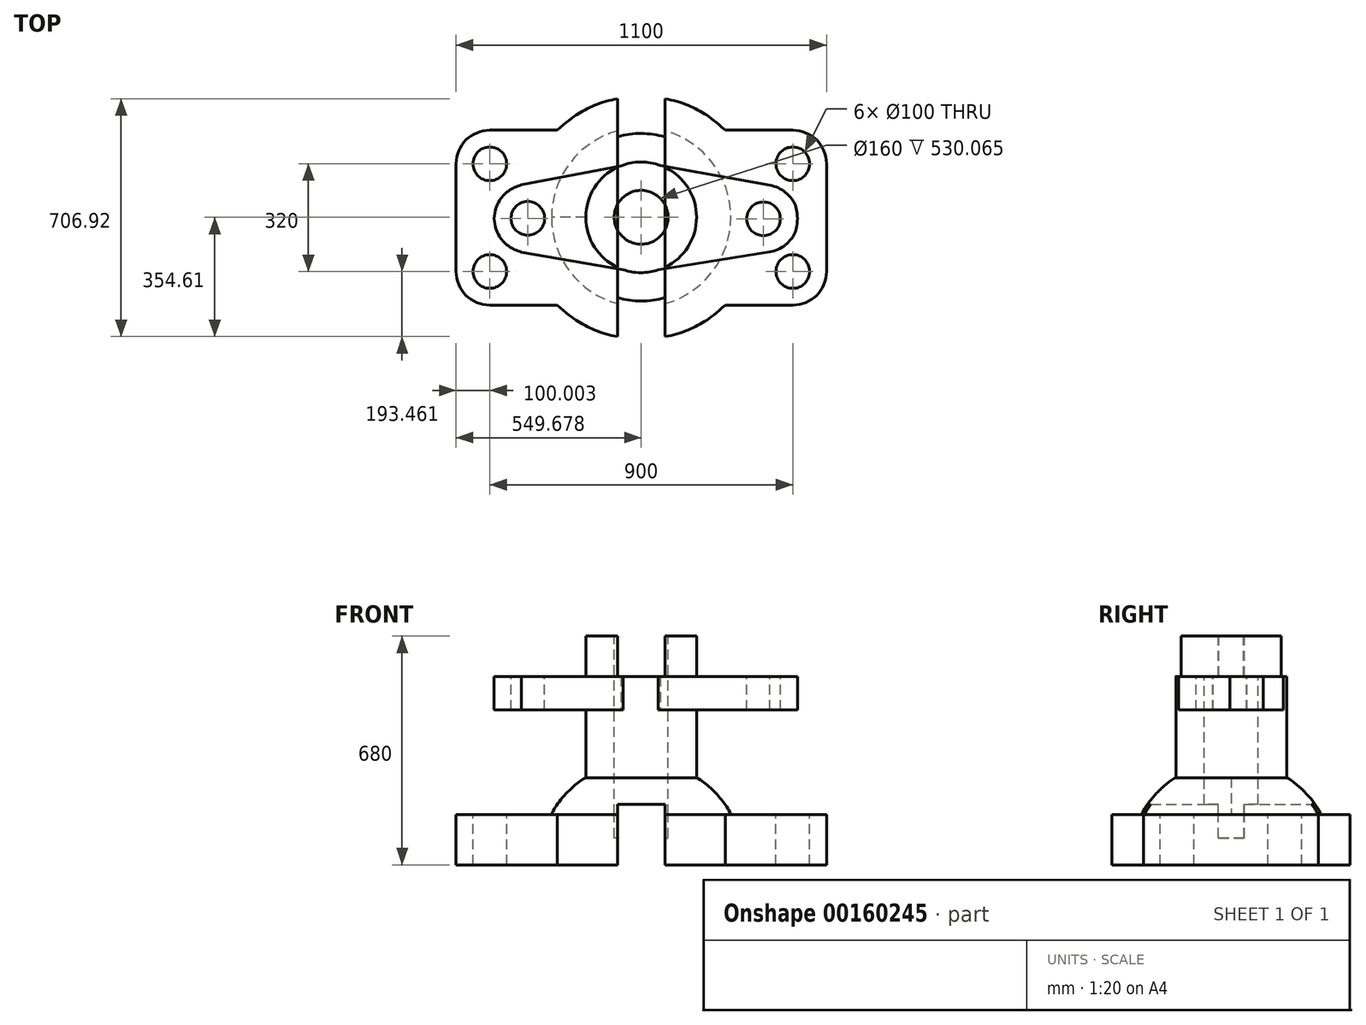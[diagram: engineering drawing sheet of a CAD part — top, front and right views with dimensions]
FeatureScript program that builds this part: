
annotation { "Feature Type Name" : "Feature", "Feature Type Description" : "" }
export const myFeature = defineFeature(function(context is Context, id is Id, definition is map)
    precondition{}
    {
        {
            var Q0;
            Q0=qCreatedBy(makeId("Top.planeOp"),FACE);
            var sketch = newSketch(context, id + "F0", { "sketchPlane" : qUnion([Q0])});
            skLineSegment(sketch, "E0.bottom", {"start": v(-555.83, 304.85) * mm, "end": v(544.17, 304.85) * mm});
            skLineSegment(sketch, "E0.top", {"start": v(-555.83, -215.15) * mm, "end": v(544.17, -215.15) * mm});
            skLineSegment(sketch, "E0.left", {"start": v(-555.83, 304.85) * mm, "end": v(-555.83, -215.15) * mm});
            skLineSegment(sketch, "E0.right", {"start": v(544.17, 304.85) * mm, "end": v(544.17, -215.15) * mm});
            skLineSegment(sketch, "E1", {"start": v(-555.83, 304.85) * mm, "end": v(-555.83, 365.16) * mm});
            skLineSegment(sketch, "E2", {"start": v(-76.07, 304.85) * mm, "end": v(-76.07, 398.31) * mm});
            skFitSpline(sketch, "E3", {"points": [v(-76.07, 398.31) * mm, v(-167.84, 368.02) * mm, v(-255.04, 304.85) * mm], "startDerivative": vector(-216.42, -35.21) * mm, "endDerivative": vector(-219.3, -200.67) * mm});
            skLineSegment(sketch, "E4", {"start": v(-5.83, 365.16) * mm, "end": v(-5.83, 347.73) * mm});
            skLineSegment(sketch, "E5.MirrorCS", {"start": v(64.42, 304.85) * mm, "end": v(64.42, 398.31) * mm});
            skFitSpline(sketch, "E6.MirrorCS", {"points": [v(64.42, 398.31) * mm, v(156.19, 368.02) * mm, v(243.39, 304.85) * mm], "startDerivative": vector(216.42, -35.21) * mm, "endDerivative": vector(219.3, -200.67) * mm});
            skLineSegment(sketch, "E7", {"start": v(544.17, 304.85) * mm, "end": v(591.2, 304.85) * mm});
            skLineSegment(sketch, "E8", {"start": v(591.2, 304.85) * mm, "end": v(591.2, 44.85) * mm});
            skLineSegment(sketch, "E9", {"start": v(591.2, 44.85) * mm, "end": v(627.35, 44.85) * mm});
            skLineSegment(sketch, "E10.MirrorCS", {"start": v(64.42, -215.15) * mm, "end": v(64.42, -308.61) * mm});
            skLineSegment(sketch, "E11.MirrorCS", {"start": v(-76.07, -215.15) * mm, "end": v(-76.07, -308.61) * mm});
            skFitSpline(sketch, "E12.MirrorCS", {"points": [v(-76.07, -308.61) * mm, v(-167.84, -278.32) * mm, v(-255.04, -215.15) * mm], "startDerivative": vector(-216.42, 35.21) * mm, "endDerivative": vector(-219.3, 200.67) * mm});
            skFitSpline(sketch, "E13.MirrorCS", {"points": [v(64.42, -308.61) * mm, v(156.19, -278.32) * mm, v(243.39, -215.15) * mm], "startDerivative": vector(216.42, 35.21) * mm, "endDerivative": vector(219.3, 200.67) * mm});
            skSolve(sketch);
        }
        {
            var Q0;
            Q0 = qSketchRegion(id + "F0", true);
            extrude(context, id + "F1", {"entities" : qUnion([Q0]), "depth" : 150 * mm});
        }
        {
            var Q0;
            Q0=makeQuery(id+"F1.opExtrude","SWEPT_EDGE",EDGE,{"disambiguationData":[OSD([sQuery(id+"F0.wireOp",EDGE,"E0.top"),sQuery(id+"F0.wireOp",EDGE,"E0.left")])]});
            fillet(context, id + "F2", {"entities" : qUnion([Q0]), "radius" : 100 * mm, "tangentPropagation" : true, "allowEdgeOverflow" : false});
        }
        {
            var Q0;
            Q0=makeQuery(id+"F1.opExtrude","SWEPT_EDGE",EDGE,{"disambiguationData":[OSD([sQuery(id+"F0.wireOp",EDGE,"E0.bottom"),sQuery(id+"F0.wireOp",EDGE,"E0.left")])]});
            fillet(context, id + "F3", {"entities" : qUnion([Q0]), "radius" : 100 * mm, "tangentPropagation" : true, "allowEdgeOverflow" : false});
        }
        {
            var Q0;
            Q0=makeQuery(id+"F1.opExtrude","SWEPT_EDGE",EDGE,{"disambiguationData":[OSD([sQuery(id+"F0.wireOp",EDGE,"E0.bottom"),sQuery(id+"F0.wireOp",EDGE,"E0.right")])]});
            fillet(context, id + "F4", {"entities" : qUnion([Q0]), "radius" : 100 * mm, "tangentPropagation" : true, "allowEdgeOverflow" : false});
        }
        {
            var Q0;
            Q0=makeQuery(id+"F1.opExtrude","SWEPT_EDGE",EDGE,{"disambiguationData":[OSD([sQuery(id+"F0.wireOp",EDGE,"E0.top"),sQuery(id+"F0.wireOp",EDGE,"E0.right")])]});
            fillet(context, id + "F5", {"entities" : qUnion([Q0]), "radius" : 100 * mm, "tangentPropagation" : true, "allowEdgeOverflow" : false});
        }
        {
            var Q0;
            Q0=makeQuery(id+"F1.opExtrude","CAP_FACE",FACE,{"disambiguationData":[OSD([sQuery(id+"F0.wireOp",EDGE,"E0.bottom"),sQuery(id+"F0.wireOp",EDGE,"E0.top"),sQuery(id+"F0.wireOp",EDGE,"E0.left"),sQuery(id+"F0.wireOp",EDGE,"E0.right"),sQuery(id+"F0.wireOp",EDGE,"E2"),sQuery(id+"F0.wireOp",EDGE,"E3"),sQuery(id+"F0.wireOp",EDGE,"E5.MirrorCS"),sQuery(id+"F0.wireOp",EDGE,"E6.MirrorCS"),sQuery(id+"F0.wireOp",EDGE,"E10.MirrorCS"),sQuery(id+"F0.wireOp",EDGE,"E11.MirrorCS"),sQuery(id+"F0.wireOp",EDGE,"E12.MirrorCS"),sQuery(id+"F0.wireOp",EDGE,"E13.MirrorCS")])],"isStart":false});
            var sketch = newSketch(context, id + "F6", { "sketchPlane" : qUnion([Q0])});
            skCircle(sketch, "E14", {"center": v(-455.83, -115.15) * mm, "radius": 50 * mm});
            skCircle(sketch, "E15.MirrorC", {"center": v(-455.83, 204.85) * mm, "radius": 50 * mm});
            skCircle(sketch, "E16.MirrorC", {"center": v(444.17, 204.85) * mm, "radius": 50 * mm});
            skCircle(sketch, "E17.MirrorC", {"center": v(444.17, -115.15) * mm, "radius": 50 * mm});
            skLineSegment(sketch, "E18.bottom", {"start": v(64.42, 304.85) * mm, "end": v(-76.07, 304.85) * mm});
            skLineSegment(sketch, "E18.top", {"start": v(64.42, -215.15) * mm, "end": v(-76.07, -215.15) * mm});
            skLineSegment(sketch, "E18.left", {"start": v(64.42, 304.85) * mm, "end": v(64.42, -215.15) * mm});
            skLineSegment(sketch, "E18.right", {"start": v(-76.07, 304.85) * mm, "end": v(-76.07, -215.15) * mm});
            skLineSegment(sketch, "E19.bottom", {"start": v(-76.07, -215.15) * mm, "end": v(64.42, -215.15) * mm});
            skLineSegment(sketch, "E19.top", {"start": v(-76.07, -261.88) * mm, "end": v(64.42, -261.88) * mm});
            skLineSegment(sketch, "E19.left", {"start": v(-76.07, -215.15) * mm, "end": v(-76.07, -261.88) * mm});
            skLineSegment(sketch, "E19.right", {"start": v(64.42, -215.15) * mm, "end": v(64.42, -261.88) * mm});
            skLineSegment(sketch, "E20.bottom", {"start": v(-76.07, 304.85) * mm, "end": v(64.42, 304.85) * mm});
            skLineSegment(sketch, "E20.top", {"start": v(-76.07, 344.13) * mm, "end": v(64.42, 344.13) * mm});
            skLineSegment(sketch, "E20.left", {"start": v(-76.07, 304.85) * mm, "end": v(-76.07, 344.13) * mm});
            skLineSegment(sketch, "E20.right", {"start": v(64.42, 304.85) * mm, "end": v(64.42, 344.13) * mm});
            skSolve(sketch);
        }
        {
            var Q0;
            Q0 = qSketchRegion(id + "F6", true);
            extrude(context, id + "F7", {"entities" : qUnion([Q0]), "operationType" : NewBodyOperationType.REMOVE, "oppositeDirection" : true, "depth" : 150 * mm});
        }
        {
            var Q0;
            Q0=qCreatedBy(makeId("Front.planeOp"),FACE);
            cPlane(context, id + "F8", {"entities" : qUnion([Q0]), "cplaneType" : CPlaneType.OFFSET, "offset" : 46 * mm, "oppositeDirection" : true, "width" : 150 * mm, "height" : 150 * mm});
        }
        {
            var Q0;
            Q0=qCreatedBy(id+"F8.planeOp",FACE);
            var sketch = newSketch(context, id + "F9", { "sketchPlane" : qUnion([Q0])});
            skLineSegment(sketch, "E21", {"start": v(-272.34, 149.93) * mm, "end": v(-6.15, 149.93) * mm});
            skLineSegment(sketch, "E22", {"start": v(-6.15, 149.93) * mm, "end": v(-6.15, 258.86) * mm});
            skLineSegment(sketch, "E23", {"start": v(-6.15, 258.86) * mm, "end": v(-170.58, 258.86) * mm});
            skFitSpline(sketch, "E24", {"points": [v(-170.58, 258.86) * mm, v(-272.34, 149.93) * mm], "startDerivative": vector(-85.18, -35) * mm, "endDerivative": vector(-40.95, -110.05) * mm});
            skSolve(sketch);
        }
        {
            var Q0;
            Q0 = qSketchRegion(id + "F9", true);
            var Q1;
            Q1=sQuery(id+"F9.wireOp",EDGE,"E22");
            revolve(context, id + "F10", {"entities" : qUnion([Q0]), "axis" : qUnion([Q1]), "revolveType" : RevolveType.FULL});
        }
        {
            var Q0;
            Q0 = qSketchRegion(id + "F6", true);
            extrude(context, id + "F11", {"entities" : qUnion([Q0]), "operationType" : NewBodyOperationType.REMOVE, "depth" : 30 * mm});
        }
        {
            var Q0;
            Q0=makeQuery(id+"F11.boolean.opBoolean","COPY",FACE,{"derivedFrom":makeQuery(id+"F11.opExtrude","CAP_FACE",FACE,{"disambiguationData":[OSD([sQuery(id+"F6.wireOp",EDGE,"E18.left"),sQuery(id+"F6.wireOp",EDGE,"E18.right"),sQuery(id+"F6.wireOp",EDGE,"E19.top"),sQuery(id+"F6.wireOp",EDGE,"E19.left"),sQuery(id+"F6.wireOp",EDGE,"E19.right"),sQuery(id+"F6.wireOp",EDGE,"E20.top"),sQuery(id+"F6.wireOp",EDGE,"E20.left"),sQuery(id+"F6.wireOp",EDGE,"E20.right")])],"isStart":true})});
            var sketch = newSketch(context, id + "F12", { "sketchPlane" : qUnion([Q0])});
            skPoint(sketch, "E25.oppositeSnap0", {"position": v(-5.82, -220.16) * mm});
            skLineSegment(sketch, "E25.bottom", {"start": v(-76.07, 332.47) * mm, "end": v(64.42, 332.47) * mm});
            skLineSegment(sketch, "E25.top", {"start": v(-76.07, -220.16) * mm, "end": v(64.42, -220.16) * mm});
            skLineSegment(sketch, "E25.left", {"start": v(-76.07, 332.47) * mm, "end": v(-76.07, -220.16) * mm});
            skLineSegment(sketch, "E25.right", {"start": v(64.42, 332.47) * mm, "end": v(64.42, -220.16) * mm});
            skLineSegment(sketch, "E26.top", {"start": v(-76.07, -241.35) * mm, "end": v(64.42, -241.35) * mm});
            skLineSegment(sketch, "E26.left", {"start": v(-76.07, -220.16) * mm, "end": v(-76.07, -241.35) * mm});
            skLineSegment(sketch, "E26.right", {"start": v(64.42, -220.16) * mm, "end": v(64.42, -241.35) * mm});
            skSolve(sketch);
        }
        {
            var Q0;
            Q0 = qSketchRegion(id + "F12", true);
            extrude(context, id + "F13", {"entities" : qUnion([Q0]), "operationType" : NewBodyOperationType.REMOVE, "oppositeDirection" : true, "depth" : 25 * mm});
        }
        {
            var Q0;
            Q0=makeQuery(id+"F11.boolean.opBoolean","COPY",FACE,{"derivedFrom":makeQuery(id+"F11.opExtrude","CAP_FACE",FACE,{"disambiguationData":[OSD([sQuery(id+"F6.wireOp",EDGE,"E18.left"),sQuery(id+"F6.wireOp",EDGE,"E18.right"),sQuery(id+"F6.wireOp",EDGE,"E19.top"),sQuery(id+"F6.wireOp",EDGE,"E19.left"),sQuery(id+"F6.wireOp",EDGE,"E19.right"),sQuery(id+"F6.wireOp",EDGE,"E20.top"),sQuery(id+"F6.wireOp",EDGE,"E20.left"),sQuery(id+"F6.wireOp",EDGE,"E20.right")])],"isStart":false})});
            var sketch = newSketch(context, id + "F14", { "sketchPlane" : qUnion([Q0])});
            skCircle(sketch, "E27", {"center": v(-6.15, -46) * mm, "radius": 164.5 * mm});
            skSolve(sketch);
        }
        {
            var Q0;
            Q0 = qSketchRegion(id + "F14", true);
            extrude(context, id + "F15", {"entities" : qUnion([Q0]), "operationType" : NewBodyOperationType.ADD, "oppositeDirection" : true, "depth" : 500 * mm});
        }
        {
            var Q0;
            Q0=makeQuery(id+"F15.opExtrude","CAP_FACE",FACE,{"disambiguationData":[OSD([sQuery(id+"F14.wireOp",EDGE,"E27")])],"isStart":false});
            var sketch = newSketch(context, id + "F16", { "sketchPlane" : qUnion([Q0])});
            skLineSegment(sketch, "E28.bottom", {"start": v(-76, 326.74) * mm, "end": v(64.94, 326.74) * mm});
            skLineSegment(sketch, "E28.top", {"start": v(-76, -249.95) * mm, "end": v(64.94, -249.95) * mm});
            skLineSegment(sketch, "E28.left", {"start": v(-76, 326.74) * mm, "end": v(-76, -249.95) * mm});
            skLineSegment(sketch, "E28.right", {"start": v(64.94, 326.74) * mm, "end": v(64.94, -249.95) * mm});
            skSolve(sketch);
        }
        {
            var Q0;
            Q0 = qSketchRegion(id + "F16", true);
            extrude(context, id + "F17", {"entities" : qUnion([Q0]), "operationType" : NewBodyOperationType.REMOVE, "oppositeDirection" : true, "depth" : 120 * mm});
        }
        {
            var Q0;
            Q0=makeQuery(id+"F17.boolean.opBoolean","COPY",FACE,{"derivedFrom":makeQuery(id+"F17.opExtrude","CAP_FACE",FACE,{"disambiguationData":[OSD([sQuery(id+"F16.wireOp",EDGE,"E28.bottom"),sQuery(id+"F16.wireOp",EDGE,"E28.top"),sQuery(id+"F16.wireOp",EDGE,"E28.left"),sQuery(id+"F16.wireOp",EDGE,"E28.right")])],"isStart":false})});
            var sketch = newSketch(context, id + "F18", { "sketchPlane" : qUnion([Q0])});
            skLineSegment(sketch, "E29", {"start": v(-6.83, 210.5) * mm, "end": v(-361.81, 142.59) * mm});
            skPoint(sketch, "E29.startSnap0", {"position": v(-5.47, 210.5) * mm});
            skFitSpline(sketch, "E30", {"points": [v(-361.81, 142.59) * mm, v(-411.19, 115.48) * mm, v(-443.67, 42.4) * mm], "startDerivative": vector(-119.27, -42.29) * mm, "endDerivative": vector(-18.86, -186.28) * mm});
            skLineSegment(sketch, "E31", {"start": v(-443.67, 42.4) * mm, "end": v(-419.41, 42.4) * mm});
            skFitSpline(sketch, "E32.MirrorCS", {"points": [v(-361.81, -57.77) * mm, v(-411.19, -30.67) * mm, v(-443.67, 42.4) * mm], "startDerivative": vector(-119.27, 42.29) * mm, "endDerivative": vector(-18.86, 186.28) * mm});
            skLineSegment(sketch, "E33", {"start": v(-6.83, -118.5) * mm, "end": v(-361.81, -57.77) * mm});
            skPoint(sketch, "E33.startSnap0", {"position": v(-5.47, -118.5) * mm});
            skLineSegment(sketch, "E34", {"start": v(-5.47, 210.5) * mm, "end": v(376.15, 141.45) * mm});
            skFitSpline(sketch, "E35", {"points": [v(376.15, 141.45) * mm, v(437.23, 105.7) * mm, v(458.14, 42.13) * mm], "startDerivative": vector(151.98, -25.75) * mm, "endDerivative": vector(8.26, -194) * mm});
            skLineSegment(sketch, "E36", {"start": v(458.14, 42.13) * mm, "end": v(415, 42.13) * mm});
            skFitSpline(sketch, "E37.MirrorCS", {"points": [v(376.15, -57.2) * mm, v(437.23, -21.45) * mm, v(458.14, 42.13) * mm], "startDerivative": vector(151.98, 25.75) * mm, "endDerivative": vector(8.26, 194) * mm});
            skLineSegment(sketch, "E38", {"start": v(-5.47, -118.5) * mm, "end": v(376.15, -57.2) * mm});
            skSolve(sketch);
        }
        {
            var Q0;
            {var subQ0=sQuery(id+"F18.wireOp",EDGE,"E30");Q0=makeQuery(id+"F18.imprint","IMPRINT",FACE,{"disambiguationData":[TD([[makeQuery(id+"F18.imprint","IMPRINT",EDGE,{"derivedFrom":subQ0}),1.0]])]});}
            var Q1;
            {var subQ0=sQuery(id+"F18.wireOp",EDGE,"E35");Q1=makeQuery(id+"F18.imprint","IMPRINT",FACE,{"disambiguationData":[TD([[makeQuery(id+"F18.imprint","IMPRINT",EDGE,{"derivedFrom":subQ0}),-1.0]])]});}
            var Q2;
            {var subQ1=sQuery(id+"F16.wireOp",EDGE,"E28.left");var subQ5=makeQuery(id+"F17.boolean.opBoolean","COPY",EDGE,{"derivedFrom":makeQuery(id+"F17.opExtrude","CAP_EDGE",EDGE,{"disambiguationData":[OSD([subQ1])],"isStart":false})});Q2=makeQuery(id+"F18.imprint","IMPRINT",FACE,{"disambiguationData":[TD([[makeQuery(id+"F18.imprint","IMPRINT",EDGE,{"derivedFrom":subQ5}),1.0]])]});}
            extrude(context, id + "F19", {"entities" : qUnion([Q0, Q1, Q2]), "operationType" : NewBodyOperationType.ADD, "oppositeDirection" : true, "depth" : 100 * mm});
        }
        {
            var Q0;
            {var subQ0=sQuery(id+"F16.wireOp",EDGE,"E28.right");var subQ1=sQuery(id+"F16.wireOp",EDGE,"E28.left");var subQ2=sQuery(id+"F16.wireOp",EDGE,"E28.top");var subQ3=sQuery(id+"F16.wireOp",EDGE,"E28.bottom");Q0=makeQuery(id+"F19.boolean.opBoolean","MERGE",FACE,{"derivedFrom":[makeQuery(id+"F17.boolean.opBoolean","COPY",FACE,{"derivedFrom":makeQuery(id+"F17.opExtrude","CAP_FACE",FACE,{"disambiguationData":[OSD([subQ3,subQ2,subQ1,subQ0])],"isStart":false})}),makeQuery(id+"F19.opExtrude","CAP_FACE",FACE,{"disambiguationData":[OSD([sQuery(id+"F14.wireOp",EDGE,"E27"),subQ3,subQ2,subQ1,subQ0,sQuery(id+"F18.wireOp",EDGE,"E29"),sQuery(id+"F18.wireOp",EDGE,"E30"),sQuery(id+"F18.wireOp",EDGE,"E32.MirrorCS"),sQuery(id+"F18.wireOp",EDGE,"E33"),sQuery(id+"F18.wireOp",EDGE,"E34"),sQuery(id+"F18.wireOp",EDGE,"E35"),sQuery(id+"F18.wireOp",EDGE,"E37.MirrorCS"),sQuery(id+"F18.wireOp",EDGE,"E38")])],"isStart":true})]});}
            var sketch = newSketch(context, id + "F20", { "sketchPlane" : qUnion([Q0])});
            skCircle(sketch, "E39", {"center": v(-342.9, 42.81) * mm, "radius": 50 * mm});
            skCircle(sketch, "E40", {"center": v(357.1, 41.45) * mm, "radius": 50 * mm});
            skSolve(sketch);
        }
        {
            var Q0;
            Q0 = qSketchRegion(id + "F20", true);
            extrude(context, id + "F21", {"entities" : qUnion([Q0]), "operationType" : NewBodyOperationType.REMOVE, "oppositeDirection" : true, "depth" : 100 * mm});
        }
        {
            var Q0;
            {var subQ0=sQuery(id+"F14.wireOp",EDGE,"E27");Q0=makeQuery(id+"F17.boolean.opBoolean","SPLIT",FACE,{"disambiguationData":[TD([makeQuery(id+"F17.opExtrude","SWEPT_FACE",FACE,{"disambiguationData":[OSD([sQuery(id+"F16.wireOp",EDGE,"E28.right")])]})])],"derivedFrom":makeQuery(id+"F15.opExtrude","CAP_FACE",FACE,{"disambiguationData":[OSD([subQ0])],"isStart":false})});}
            var sketch = newSketch(context, id + "F22", { "sketchPlane" : qUnion([Q0])});
            skCircle(sketch, "E41", {"center": v(-6.15, 46) * mm, "radius": 80 * mm});
            skSolve(sketch);
        }
        {
            var Q0;
            Q0 = qSketchRegion(id + "F22", true);
            extrude(context, id + "F23", {"entities" : qUnion([Q0]), "operationType" : NewBodyOperationType.REMOVE, "oppositeDirection" : true, "depth" : 600 * mm});
        }
    });
